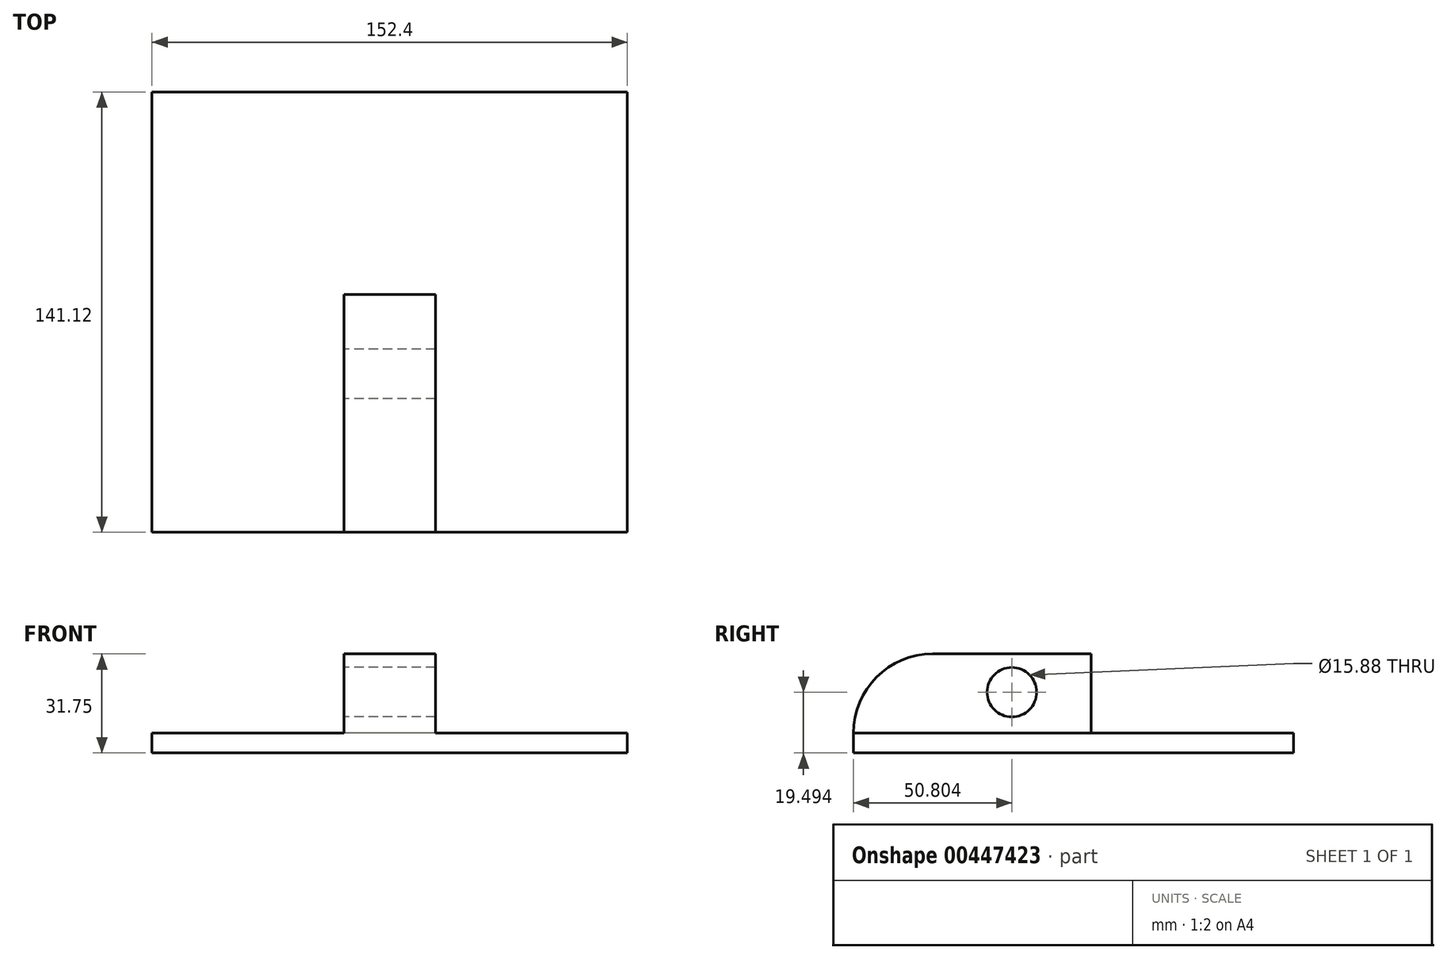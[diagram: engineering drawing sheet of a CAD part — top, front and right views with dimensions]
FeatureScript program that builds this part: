
annotation { "Feature Type Name" : "Feature", "Feature Type Description" : "" }
export const myFeature = defineFeature(function(context is Context, id is Id, definition is map)
    precondition{}
    {
        {
            var Q0;
            Q0=qCreatedBy(makeId("Top.planeOp"),FACE);
            var sketch = newSketch(context, id + "F0", { "sketchPlane" : qUnion([Q0])});
            skLineSegment(sketch, "E0.bottom", {"start": v(76.2, 70.56) * mm, "end": v(-76.2, 70.56) * mm});
            skLineSegment(sketch, "E0.top", {"start": v(76.2, -70.56) * mm, "end": v(-76.2, -70.56) * mm});
            skLineSegment(sketch, "E0.left", {"start": v(76.2, 70.56) * mm, "end": v(76.2, -70.56) * mm});
            skLineSegment(sketch, "E0.right", {"start": v(-76.2, 70.56) * mm, "end": v(-76.2, -70.56) * mm});
            skPoint(sketch, "E0.middle", {"position": v(0, 0) * mm});
            skSolve(sketch);
        }
        {
            var Q0;
            Q0=makeQuery(id+"F0.imprint","IMPRINT",FACE,{"disambiguationData":[TD([[makeQuery(id+"F0.imprint","IMPRINT",EDGE,{"derivedFrom":sQuery(id+"F0.wireOp",EDGE,"E0.bottom")}),1.0]])]});
            extrude(context, id + "F1", {"entities" : qUnion([Q0]), "depth" : 6.35 * mm});
        }
        {
            var Q0;
            Q0=makeQuery(id+"F1.opExtrude","CAP_FACE",FACE,{"disambiguationData":[OSD([sQuery(id+"F0.wireOp",EDGE,"E0.bottom"),sQuery(id+"F0.wireOp",EDGE,"E0.top"),sQuery(id+"F0.wireOp",EDGE,"E0.left"),sQuery(id+"F0.wireOp",EDGE,"E0.right")])],"isStart":false});
            var sketch = newSketch(context, id + "F2", { "sketchPlane" : qUnion([Q0])});
            skLineSegment(sketch, "E1.top", {"start": v(76.2, 5.64) * mm, "end": v(-76.2, 5.64) * mm});
            skLineSegment(sketch, "E1.left", {"start": v(76.2, -5.64) * mm, "end": v(76.2, 5.64) * mm});
            skLineSegment(sketch, "E1.right", {"start": v(-76.2, -5.64) * mm, "end": v(-76.2, 5.64) * mm});
            skPoint(sketch, "E1.middle", {"position": v(0, 0) * mm});
            skLineSegment(sketch, "E2", {"start": v(0, 5.64) * mm, "end": v(0, -70.56) * mm});
            skLineSegment(sketch, "E3.bottom", {"start": v(14.67, 5.64) * mm, "end": v(-14.67, 5.64) * mm});
            skLineSegment(sketch, "E3.top", {"start": v(14.67, -70.56) * mm, "end": v(-14.67, -70.56) * mm});
            skLineSegment(sketch, "E3.left", {"start": v(14.67, 5.64) * mm, "end": v(14.67, -70.56) * mm});
            skLineSegment(sketch, "E3.right", {"start": v(-14.67, 5.64) * mm, "end": v(-14.67, -70.56) * mm});
            skPoint(sketch, "E3.middle", {"position": v(0, -32.46) * mm});
            skLineSegment(sketch, "E4", {"start": v(-40.07, 5.64) * mm, "end": v(-40.07, -70.56) * mm});
            skLineSegment(sketch, "E5", {"start": v(40.07, 5.64) * mm, "end": v(40.07, -70.56) * mm});
            skLineSegment(sketch, "E6", {"start": v(-76.2, -45.16) * mm, "end": v(76.2, -45.16) * mm});
            skSolve(sketch);
        }
        {
            var Q0;
            {var subQ0=sQuery(id+"F2.wireOp",EDGE,"E3.bottom");var subQ1=sQuery(id+"F2.wireOp",EDGE,"E2");var subQ2=makeQuery(id+"F2.imprint","INTERSECT",VERTEX,{"derivedFrom":[subQ1,subQ0]});Q0=makeQuery(id+"F2.imprint","IMPRINT",FACE,{"disambiguationData":[TD([[makeQuery(id+"F2.imprint","IMPRINT",EDGE,{"disambiguationData":[TD([[subQ2,-1.0]])],"derivedFrom":subQ1}),-1.0]])]});}
            var Q1;
            {var subQ0=sQuery(id+"F2.wireOp",EDGE,"E3.bottom");var subQ1=sQuery(id+"F2.wireOp",EDGE,"E2");var subQ2=makeQuery(id+"F2.imprint","INTERSECT",VERTEX,{"derivedFrom":[subQ1,subQ0]});Q1=makeQuery(id+"F2.imprint","IMPRINT",FACE,{"disambiguationData":[TD([[makeQuery(id+"F2.imprint","IMPRINT",EDGE,{"disambiguationData":[TD([[subQ2,-1.0]])],"derivedFrom":subQ1}),1.0]])]});}
            extrude(context, id + "F3", {"entities" : qUnion([Q0, Q1]), "operationType" : NewBodyOperationType.ADD, "depth" : 25.4 * mm});
        }
        {
            var Q0;
            Q0=makeQuery(id+"F3.opExtrude","CAP_EDGE",EDGE,{"disambiguationData":[OSD([sQuery(id+"F2.wireOp",EDGE,"E3.top")])],"isStart":false});
            var Q1;
            Q1=makeQuery(id+"F3.opExtrude","CAP_EDGE",EDGE,{"disambiguationData":[OSD([sQuery(id+"F2.wireOp",EDGE,"E3.bottom")])],"isStart":false});
            var Q2;
            Q2=makeQuery(id+"F3.opExtrude","CAP_EDGE",EDGE,{"disambiguationData":[OSD([sQuery(id+"F2.wireOp",EDGE,"E6")])],"isStart":false});
            fillet(context, id + "F4", {"entities" : qUnion([Q0, Q1, Q2]), "radius" : 25.4 * mm, "tangentPropagation" : true, "allowEdgeOverflow" : false});
        }
        {
            var Q0;
            Q0=makeQuery(id+"F3.opExtrude","SWEPT_FACE",FACE,{"disambiguationData":[OSD([sQuery(id+"F2.wireOp",EDGE,"E3.right")])]});
            var sketch = newSketch(context, id + "F5", { "sketchPlane" : qUnion([Q0])});
            skLineSegment(sketch, "E7", {"start": v(19.76, 31.75) * mm, "end": v(19.76, 6.35) * mm});
            skCircle(sketch, "E8", {"center": v(19.76, 19.5) * mm, "radius": 7.94 * mm});
            skSolve(sketch);
        }
        {
            var Q0;
            {var subQ0=sQuery(id+"F5.wireOp",EDGE,"E8");var subQ1=sQuery(id+"F5.wireOp",EDGE,"E7");var subQ2=makeQuery(id+"F5.imprint","INTERSECT",VERTEX,{"disambiguationData":[OD(0.0)],"derivedFrom":[subQ1,subQ0]});Q0=makeQuery(id+"F5.imprint","IMPRINT",FACE,{"disambiguationData":[TD([[makeQuery(id+"F5.imprint","IMPRINT",EDGE,{"disambiguationData":[TD([[subQ2,-1.0]])],"derivedFrom":subQ1}),-1.0]])]});}
            var Q1;
            {var subQ0=sQuery(id+"F5.wireOp",EDGE,"E8");var subQ1=sQuery(id+"F5.wireOp",EDGE,"E7");var subQ2=makeQuery(id+"F5.imprint","INTERSECT",VERTEX,{"disambiguationData":[OD(0.0)],"derivedFrom":[subQ1,subQ0]});Q1=makeQuery(id+"F5.imprint","IMPRINT",FACE,{"disambiguationData":[TD([[makeQuery(id+"F5.imprint","IMPRINT",EDGE,{"disambiguationData":[TD([[subQ2,-1.0]])],"derivedFrom":subQ1}),1.0]])]});}
            extrude(context, id + "F6", {"entities" : qUnion([Q0, Q1]), "operationType" : NewBodyOperationType.REMOVE, "oppositeDirection" : true, "depth" : 76.2 * mm});
        }
    });
